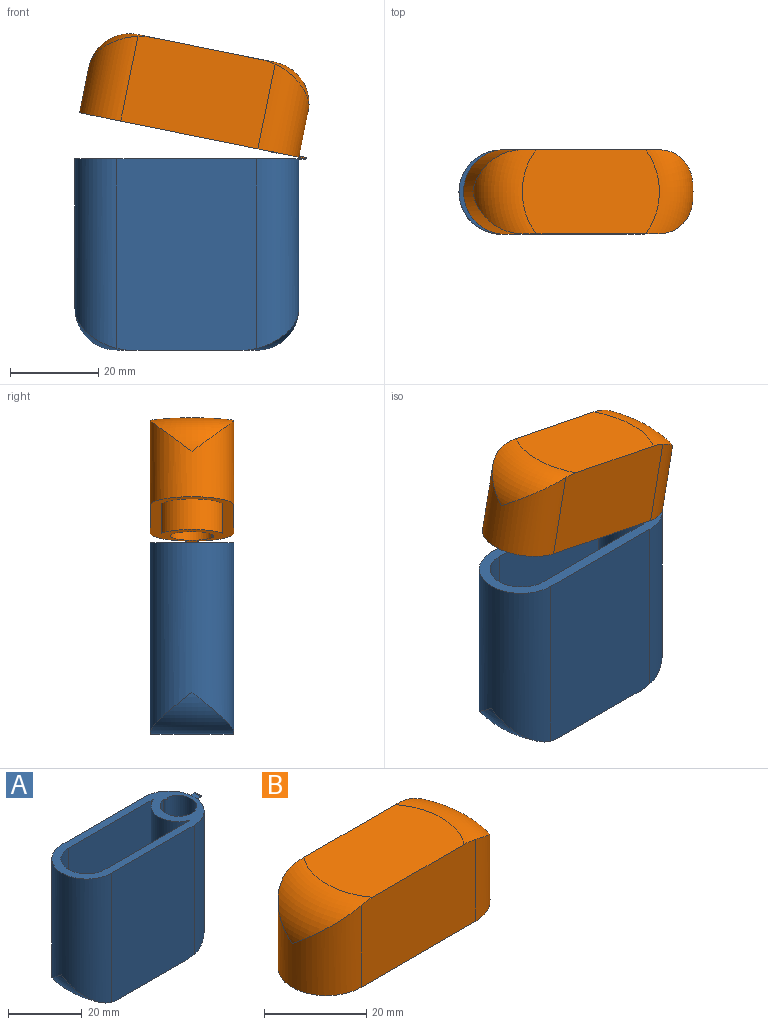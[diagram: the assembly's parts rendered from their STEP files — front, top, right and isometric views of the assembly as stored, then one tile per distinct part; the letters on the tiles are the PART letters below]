
ASSEMBLY  parts=2 mates=1
PART A: 25 faces, bbox 55.1x33.1x43.7 mm
  f0: cylinder r=4.95mm len=10.74mm, axis (0,0,1), area 317.9mm2, adj f9,f19,f20
  f1: plane 8.9x8.9mm, normal (0,0,1), area 62.2mm2, adj f20
  f2: cylinder r=9.53mm len=43.03mm, axis (0,0,-1), area 1170.5mm2, adj f3,f5,f8,f9,f21,f23,f24
  f3: plane 43.56x31.92mm, normal (0,1,0), area 1377.2mm2, adj f2,f4,f6,f7,f8,f9
  f4: cylinder r=9.53mm len=43.03mm, axis (0,0,-1), area 1170.7mm2, adj f3,f5,f7,f9
  f5: plane 43.56x31.92mm, normal (0,-1,0), area 1377.2mm2, adj f2,f4,f6,f7,f8,f9
  f6: plane 31.75x19.05mm, normal (0,0,-1), area 566.3mm2, adj f3,f5,f7,f8
  f7: torus R=15.88mm, axis (0,0,1), area 209.4mm2, adj f3,f4,f5,f6
  f8: torus R=15.88mm, axis (0,0,1), area 209.4mm2, adj f2,f3,f5,f6
  f9: plane 52.18x19.05mm, normal (0,0,1), area 329.7mm2, adj f0,f2,f3,f4,f5,f10,f11,f12
  f10: cylinder r=7.03mm len=40.74mm, axis (0,0,-1), area 557.5mm2, adj f9,f11,f13,f16,f17,f18
  f11: plane 40.94x31.79mm, normal (0,-1,0), area 1298.4mm2, adj f9,f10,f12,f14,f15,f16
  f12: cylinder r=7.03mm len=40.74mm, axis (0,0,-1), area 836.2mm2, adj f9,f11,f13,f15
  f13: plane 40.94x31.79mm, normal (0,1,0), area 1298.4mm2, adj f9,f10,f12,f14,f15,f16
  f14: plane 31.75x14.05mm, normal (0,0,1), area 431.1mm2, adj f11,f13,f15,f16
  f15: torus R=15.88mm, axis (0,0,1), area 109.7mm2, adj f11,f12,f13,f14
  f16: torus R=15.88mm, axis (0,0,1), area 109.7mm2, adj f10,f11,f13,f14
  f17: cylinder r=7.45mm len=13.94mm, axis (0,0,1), area 247.6mm2, adj f9,f10,f18
  f18: plane 13.94x10.95mm, normal (0,0,-1), area 113.8mm2, adj f10,f17
  f19: cylinder r=0.86mm len=11.24mm, axis (0,0,1), area 20.4mm2, adj f0,f9,f20
  f20: torus R=4.45mm, axis (0,0,1), area 22.6mm2, adj f0,f1,f19
  f21: plane 2.54x1.59mm, normal (0,0,-1), area 3.9mm2, adj f2,f22,f23,f24
  f22: cylinder r=0.13mm len=2.54mm, axis (0,1,0), area 1.7mm2, adj f9,f21,f23,f24
  f23: plane 1.71x0.25mm, normal (0,-1,0), area 0.2mm2, adj f2,f9,f21,f22
  f24: plane 1.71x0.25mm, normal (0,1,0), area 0.2mm2, adj f2,f9,f21,f22
PART B: 29 faces, bbox 55.1x33.1x20.3 mm
  f0: cylinder r=4.95mm len=10.74mm, axis (0,0,1), area 317.9mm2, adj f2,f21,f23
  f1: plane 8.9x8.9mm, normal (0,0,-1), area 62.2mm2, adj f23
  f2: plane 52.03x19.05mm, normal (0,0,-1), area 328.7mm2, adj f0,f6,f7,f8,f9,f10,f14,f15
  f3: torus R=15.88mm, axis (0,0,1), area 209.4mm2, adj f4,f6,f7,f8
  f4: plane 31.75x19.05mm, normal (0,0,1), area 566.3mm2, adj f3,f5,f6,f8
  f5: torus R=15.88mm, axis (0,0,1), area 209.4mm2, adj f4,f6,f8,f9
  f6: plane 31.92x20.16mm, normal (0,-1,0), area 634.2mm2, adj f2,f3,f4,f5,f7,f9
  f7: cylinder r=9.53mm len=19.63mm, axis (0,0,-1), area 470.5mm2, adj f2,f3,f6,f8
  f8: plane 31.92x20.16mm, normal (0,1,0), area 634.2mm2, adj f2,f3,f4,f5,f7,f9
  f9: cylinder r=9.53mm len=19.63mm, axis (0,0,-1), area 469.8mm2, adj f2,f5,f6,f8,f26,f27,f28
  f10: cylinder r=7.03mm len=17.34mm, axis (0,0,-1), area 27mm2, adj f2,f13,f14,f18,f19
  f11: torus R=15.88mm, axis (0,0,1), area 109.7mm2, adj f12,f14,f15,f16
  f12: plane 31.75x14.05mm, normal (0,0,-1), area 431.1mm2, adj f11,f13,f14,f16
  f13: torus R=15.88mm, axis (0,0,1), area 96.2mm2, adj f10,f12,f14,f16,f17,f19
  f14: plane 31.79x17.54mm, normal (0,1,0), area 555.5mm2, adj f2,f10,f11,f12,f13,f15
  f15: cylinder r=7.03mm len=17.34mm, axis (0,0,-1), area 319.8mm2, adj f2,f11,f14,f16
  f16: plane 31.79x17.54mm, normal (0,-1,0), area 555.5mm2, adj f2,f11,f12,f13,f15,f17
  f17: cylinder r=7.03mm len=17.34mm, axis (0,0,-1), area 27mm2, adj f2,f13,f16,f18,f19
  f18: cylinder r=7.45mm len=13.94mm, axis (0,0,1), area 247.6mm2, adj f2,f10,f17,f19
  f19: plane 13.94x10.15mm, normal (0,0,1), area 109.6mm2, adj f10,f13,f17,f18
  f20: cylinder r=4.95mm len=1.5mm, axis (0,0,-1), area 0.2mm2, adj f2,f21,f22
  f21: cylinder r=0.86mm len=11.34mm, axis (0,0,-1), area 20.6mm2, adj f0,f20,f22,f23
  f22: plane 1.5x0.5mm, normal (0,0,-1), area 0.5mm2, adj f20,f21
  f23: torus R=4.45mm, axis (0,0,1), area 22.6mm2, adj f0,f1,f21
  f24: cylinder r=0.28mm len=2.54mm, axis (0,1,0), area 2mm2, adj f2,f25,f27,f28
  f25: plane 2.54x0.27mm, normal (1,0,0), area 0.7mm2, adj f24,f26,f27,f28
  f26: plane 2.54x1.86mm, normal (0,0,1), area 4.6mm2, adj f9,f25,f27,f28
  f27: plane 1.86x0.27mm, normal (0,-1,0), area 0.4mm2, adj f2,f9,f24,f25,f26
  f28: plane 1.86x0.27mm, normal (0,1,0), area 0.4mm2, adj f2,f9,f24,f25,f26
PLACE A t=(0,0,31.75)mm
PLACE B rot(axis=(0,1,0),11.5deg) t=(-1.79,0,37.32)mm
MATE revolute B.f24 <-> A.f22  axis (0,1,0) through (26.9,-1.27,43.45)mm
